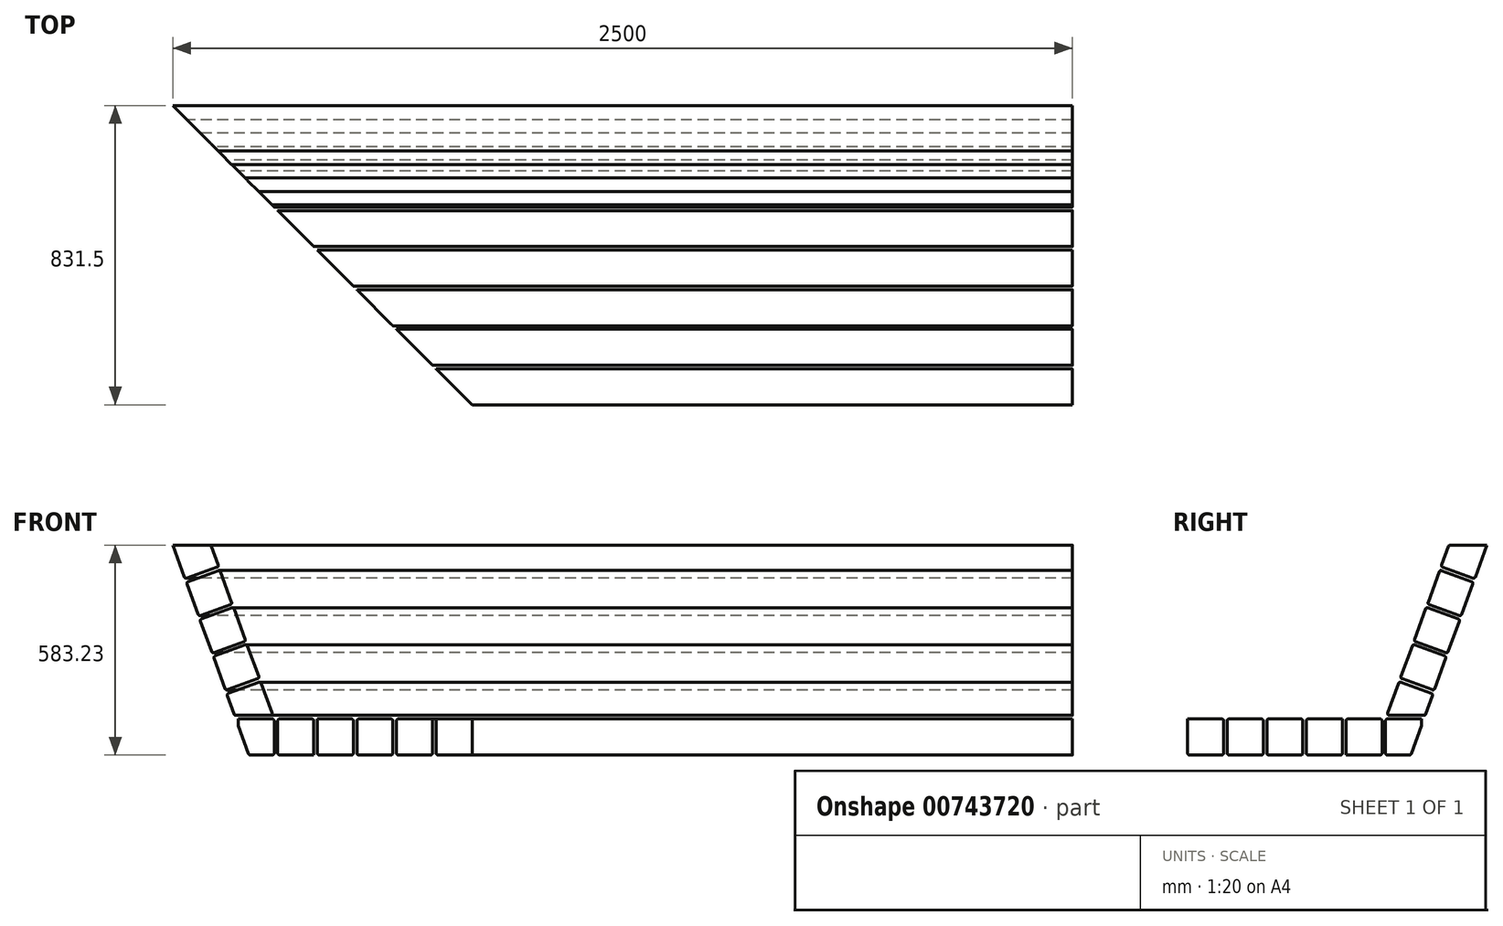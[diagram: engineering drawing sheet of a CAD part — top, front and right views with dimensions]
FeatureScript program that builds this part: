
annotation { "Feature Type Name" : "Feature", "Feature Type Description" : "" }
export const myFeature = defineFeature(function(context is Context, id is Id, definition is map)
    precondition{}
    {
        {
            var Q0;
            Q0=qCreatedBy(makeId("Right.planeOp"),FACE);
            var sketch = newSketch(context, id + "F0", { "sketchPlane" : qUnion([Q0])});
            skLineSegment(sketch, "E0.bottom", {"start": v(0, 0) * mm, "end": v(-95, 0) * mm});
            skLineSegment(sketch, "E0.top", {"start": v(-33.48, -100) * mm, "end": v(-95, -100) * mm});
            skLineSegment(sketch, "E0.left", {"start": v(0, 0) * mm, "end": v(0, -16.75) * mm});
            skLineSegment(sketch, "E0.right", {"start": v(-100, -5) * mm, "end": v(-100, -95) * mm});
            skLineSegment(sketch, "E1.1.0.0", {"start": v(-115, 0) * mm, "end": v(-205, 0) * mm});
            skLineSegment(sketch, "E1.1.0.1", {"start": v(-210, -5) * mm, "end": v(-210, -100) * mm});
            skLineSegment(sketch, "E1.1.0.2", {"start": v(-115, -100) * mm, "end": v(-210, -100) * mm});
            skLineSegment(sketch, "E1.1.0.3", {"start": v(-110, -5) * mm, "end": v(-110, -95) * mm});
            skLineSegment(sketch, "E1.2.0.0", {"start": v(-220, 0) * mm, "end": v(-315, 0) * mm});
            skLineSegment(sketch, "E1.2.0.1", {"start": v(-320, -5) * mm, "end": v(-320, -95) * mm});
            skLineSegment(sketch, "E1.2.0.2", {"start": v(-225, -100) * mm, "end": v(-315, -100) * mm});
            skLineSegment(sketch, "E1.2.0.3", {"start": v(-220, 0) * mm, "end": v(-220, -95) * mm});
            skLineSegment(sketch, "E1.3.0.0", {"start": v(-335, 0) * mm, "end": v(-425, 0) * mm});
            skLineSegment(sketch, "E1.3.0.1", {"start": v(-430, -5) * mm, "end": v(-430, -95) * mm});
            skLineSegment(sketch, "E1.3.0.2", {"start": v(-335, -100) * mm, "end": v(-425, -100) * mm});
            skLineSegment(sketch, "E1.3.0.3", {"start": v(-330, -5) * mm, "end": v(-330, -95) * mm});
            skLineSegment(sketch, "E1.4.0.0", {"start": v(-445, 0) * mm, "end": v(-535, 0) * mm});
            skLineSegment(sketch, "E1.4.0.1", {"start": v(-540, -5) * mm, "end": v(-540, -95) * mm});
            skLineSegment(sketch, "E1.4.0.2", {"start": v(-445, -100) * mm, "end": v(-535, -100) * mm});
            skLineSegment(sketch, "E1.4.0.3", {"start": v(-440, -5) * mm, "end": v(-440, -95) * mm});
            skLineSegment(sketch, "E1.5.0.0", {"start": v(-555, 0) * mm, "end": v(-650, 0) * mm});
            skLineSegment(sketch, "E1.5.0.1", {"start": v(-650, 0) * mm, "end": v(-650, -95) * mm});
            skLineSegment(sketch, "E1.5.0.2", {"start": v(-555, -100) * mm, "end": v(-645, -100) * mm});
            skLineSegment(sketch, "E1.5.0.3", {"start": v(-550, -5) * mm, "end": v(-550, -95) * mm});
            skLineSegment(sketch, "E1.direction1", {"start": v(-100, 0) * mm, "end": v(-210, 0) * mm, "construction": true});
            skLineSegment(sketch, "E2", {"start": v(-93.92, 16.71) * mm, "end": v(-63.87, 99.27) * mm});
            skLineSegment(sketch, "E3", {"start": v(-89.22, 10) * mm, "end": v(6.56, 10) * mm});
            skLineSegment(sketch, "E4", {"start": v(-57.46, 102.26) * mm, "end": v(27.11, 71.48) * mm});
            skLineSegment(sketch, "E5", {"start": v(30.1, 65.07) * mm, "end": v(11.25, 13.29) * mm});
            skPoint(sketch, "E6.orphan", {"position": v(0, -17.63) * mm});
            skLineSegment(sketch, "E7", {"start": v(-54.04, 111.66) * mm, "end": v(29.82, 81.13) * mm});
            skLineSegment(sketch, "E8", {"start": v(36.23, 84.12) * mm, "end": v(67.01, 168.7) * mm});
            skLineSegment(sketch, "E9", {"start": v(64.03, 175.1) * mm, "end": v(-19.84, 205.63) * mm});
            skLineSegment(sketch, "E10.trimOffspring", {"start": v(-57.03, 118.06) * mm, "end": v(-26.25, 202.64) * mm});
            skLineSegment(sketch, "E11", {"start": v(-19.4, 221.43) * mm, "end": v(11.38, 306) * mm});
            skLineSegment(sketch, "E12", {"start": v(181.55, 483.38) * mm, "end": v(149.1, 394.22) * mm});
            skLineSegment(sketch, "E13", {"start": v(-16.42, 215.02) * mm, "end": v(67.45, 184.5) * mm});
            skLineSegment(sketch, "E14", {"start": v(17.78, 309) * mm, "end": v(101.65, 278.47) * mm});
            skLineSegment(sketch, "E15", {"start": v(21.2, 318.39) * mm, "end": v(105.07, 287.86) * mm});
            skLineSegment(sketch, "E16", {"start": v(55.4, 412.36) * mm, "end": v(139.27, 381.83) * mm});
            skLineSegment(sketch, "E17", {"start": v(58.83, 421.75) * mm, "end": v(142.7, 391.23) * mm});
            skLineSegment(sketch, "E18", {"start": v(181.5, 483.23) * mm, "end": v(79.38, 483.23) * mm});
            skLineSegment(sketch, "E19.trimOffspring", {"start": v(142.26, 375.43) * mm, "end": v(111.48, 290.85) * mm});
            skLineSegment(sketch, "E20.trimOffspring", {"start": v(55.84, 428.16) * mm, "end": v(74.68, 479.94) * mm});
            skLineSegment(sketch, "E21.trimOffspring", {"start": v(18.22, 324.8) * mm, "end": v(49, 409.37) * mm});
            skLineSegment(sketch, "E22.trimOffspring", {"start": v(104.64, 272.06) * mm, "end": v(73.85, 187.49) * mm});
            skLineSegment(sketch, "E23", {"start": v(-0.3, -18.46) * mm, "end": v(-28.78, -96.71) * mm});
            skPoint(sketch, "E24.orphan", {"position": v(0, -100) * mm});
            skArc(sketch, "E25.filletArc", {"start": v(-650, -95) * mm, "mid": v(-648.54, -98.54) * mm, "end": v(-645, -100) * mm});
            skPoint(sketch, "E26.visualSharp", {"position": v(-550, -100) * mm});
            skArc(sketch, "E26.filletArc", {"start": v(-555, -100) * mm, "mid": v(-551.46, -98.54) * mm, "end": v(-550, -95) * mm});
            skPoint(sketch, "E27.visualSharp", {"position": v(-550, 0) * mm});
            skArc(sketch, "E27.filletArc", {"start": v(-550, -5) * mm, "mid": v(-551.46, -1.46) * mm, "end": v(-555, 0) * mm});
            skPoint(sketch, "E28.visualSharp", {"position": v(-540, 0) * mm});
            skArc(sketch, "E28.filletArc", {"start": v(-535, 0) * mm, "mid": v(-538.54, -1.46) * mm, "end": v(-540, -5) * mm});
            skPoint(sketch, "E29.visualSharp", {"position": v(-540, -100) * mm});
            skArc(sketch, "E29.filletArc", {"start": v(-540, -95) * mm, "mid": v(-538.54, -98.54) * mm, "end": v(-535, -100) * mm});
            skPoint(sketch, "E30.visualSharp", {"position": v(-440, 0) * mm});
            skArc(sketch, "E30.filletArc", {"start": v(-440, -5) * mm, "mid": v(-441.46, -1.46) * mm, "end": v(-445, 0) * mm});
            skPoint(sketch, "E31.visualSharp", {"position": v(-430, 0) * mm});
            skArc(sketch, "E31.filletArc", {"start": v(-425, 0) * mm, "mid": v(-428.54, -1.46) * mm, "end": v(-430, -5) * mm});
            skPoint(sketch, "E32.visualSharp", {"position": v(-440, -100) * mm});
            skArc(sketch, "E32.filletArc", {"start": v(-445, -100) * mm, "mid": v(-441.46, -98.54) * mm, "end": v(-440, -95) * mm});
            skPoint(sketch, "E33.visualSharp", {"position": v(-430, -100) * mm});
            skArc(sketch, "E33.filletArc", {"start": v(-430, -95) * mm, "mid": v(-428.54, -98.54) * mm, "end": v(-425, -100) * mm});
            skPoint(sketch, "E34.visualSharp", {"position": v(-330, 0) * mm});
            skArc(sketch, "E34.filletArc", {"start": v(-330, -5) * mm, "mid": v(-331.46, -1.46) * mm, "end": v(-335, 0) * mm});
            skPoint(sketch, "E35.visualSharp", {"position": v(-330, -100) * mm});
            skArc(sketch, "E35.filletArc", {"start": v(-335, -100) * mm, "mid": v(-331.46, -98.54) * mm, "end": v(-330, -95) * mm});
            skPoint(sketch, "E36.visualSharp", {"position": v(-320, 0) * mm});
            skArc(sketch, "E36.filletArc", {"start": v(-315, 0) * mm, "mid": v(-318.54, -1.46) * mm, "end": v(-320, -5) * mm});
            skPoint(sketch, "E37.visualSharp", {"position": v(-320, -100) * mm});
            skArc(sketch, "E37.filletArc", {"start": v(-320, -95) * mm, "mid": v(-318.54, -98.54) * mm, "end": v(-315, -100) * mm});
            skPoint(sketch, "E38.visualSharp", {"position": v(-220, -100) * mm});
            skArc(sketch, "E38.filletArc", {"start": v(-225, -100) * mm, "mid": v(-221.46, -98.54) * mm, "end": v(-220, -95) * mm});
            skPoint(sketch, "E39.visualSharp", {"position": v(-210, 0) * mm});
            skArc(sketch, "E39.filletArc", {"start": v(-205, 0) * mm, "mid": v(-208.54, -1.46) * mm, "end": v(-210, -5) * mm});
            skPoint(sketch, "E40.visualSharp", {"position": v(-110, -100) * mm});
            skArc(sketch, "E40.filletArc", {"start": v(-115, -100) * mm, "mid": v(-111.46, -98.54) * mm, "end": v(-110, -95) * mm});
            skPoint(sketch, "E41.visualSharp", {"position": v(-110, 0) * mm});
            skArc(sketch, "E41.filletArc", {"start": v(-110, -5) * mm, "mid": v(-111.46, -1.46) * mm, "end": v(-115, 0) * mm});
            skPoint(sketch, "E42.visualSharp", {"position": v(-100, -100) * mm});
            skArc(sketch, "E42.filletArc", {"start": v(-100, -95) * mm, "mid": v(-98.54, -98.54) * mm, "end": v(-95, -100) * mm});
            skPoint(sketch, "E43.visualSharp", {"position": v(-29.98, -100) * mm});
            skArc(sketch, "E43.filletArc", {"start": v(-33.48, -100) * mm, "mid": v(-30.61, -99.1) * mm, "end": v(-28.78, -96.71) * mm});
            skPoint(sketch, "E44.visualSharp", {"position": v(-100, 0) * mm});
            skArc(sketch, "E44.filletArc", {"start": v(-95, 0) * mm, "mid": v(-98.54, -1.46) * mm, "end": v(-100, -5) * mm});
            skArc(sketch, "E45.filletArc", {"start": v(-0.3, -18.46) * mm, "mid": v(-0.08, -17.62) * mm, "end": v(0, -16.75) * mm});
            skPoint(sketch, "E46.visualSharp", {"position": v(-96.36, 10) * mm});
            skArc(sketch, "E46.filletArc", {"start": v(-93.92, 16.71) * mm, "mid": v(-93.32, 12.13) * mm, "end": v(-89.22, 10) * mm});
            skPoint(sketch, "E47.visualSharp", {"position": v(10.06, 10) * mm});
            skArc(sketch, "E47.filletArc", {"start": v(6.56, 10) * mm, "mid": v(9.42, 10.9) * mm, "end": v(11.25, 13.29) * mm});
            skPoint(sketch, "E48.visualSharp", {"position": v(-62.16, 103.97) * mm});
            skArc(sketch, "E48.filletArc", {"start": v(-57.46, 102.26) * mm, "mid": v(-61.28, 102.1) * mm, "end": v(-63.87, 99.27) * mm});
            skPoint(sketch, "E49.visualSharp", {"position": v(34.52, 79.42) * mm});
            skArc(sketch, "E49.filletArc", {"start": v(29.82, 81.13) * mm, "mid": v(33.65, 81.3) * mm, "end": v(36.23, 84.12) * mm});
            skPoint(sketch, "E50.visualSharp", {"position": v(-58.74, 113.37) * mm});
            skArc(sketch, "E50.filletArc", {"start": v(-57.03, 118.06) * mm, "mid": v(-56.86, 114.24) * mm, "end": v(-54.04, 111.66) * mm});
            skPoint(sketch, "E51.visualSharp", {"position": v(31.81, 69.77) * mm});
            skArc(sketch, "E51.filletArc", {"start": v(30.1, 65.07) * mm, "mid": v(29.93, 68.9) * mm, "end": v(27.11, 71.48) * mm});
            skPoint(sketch, "E52.visualSharp", {"position": v(68.72, 173.4) * mm});
            skArc(sketch, "E52.filletArc", {"start": v(67.01, 168.7) * mm, "mid": v(66.85, 172.52) * mm, "end": v(64.03, 175.1) * mm});
            skPoint(sketch, "E53.visualSharp", {"position": v(-21.12, 216.73) * mm});
            skArc(sketch, "E53.filletArc", {"start": v(-19.4, 221.43) * mm, "mid": v(-19.24, 217.6) * mm, "end": v(-16.42, 215.02) * mm});
            skPoint(sketch, "E54.visualSharp", {"position": v(-24.54, 207.34) * mm});
            skArc(sketch, "E54.filletArc", {"start": v(-19.84, 205.63) * mm, "mid": v(-23.66, 205.46) * mm, "end": v(-26.25, 202.64) * mm});
            skPoint(sketch, "E55.visualSharp", {"position": v(72.14, 182.79) * mm});
            skArc(sketch, "E55.filletArc", {"start": v(67.45, 184.5) * mm, "mid": v(71.27, 184.67) * mm, "end": v(73.85, 187.49) * mm});
            skPoint(sketch, "E56.visualSharp", {"position": v(106.35, 276.76) * mm});
            skArc(sketch, "E56.filletArc", {"start": v(104.64, 272.06) * mm, "mid": v(104.47, 275.88) * mm, "end": v(101.65, 278.47) * mm});
            skPoint(sketch, "E57.visualSharp", {"position": v(109.77, 286.15) * mm});
            skArc(sketch, "E57.filletArc", {"start": v(105.07, 287.86) * mm, "mid": v(108.9, 288.03) * mm, "end": v(111.48, 290.85) * mm});
            skPoint(sketch, "E58.visualSharp", {"position": v(16.5, 320.1) * mm});
            skArc(sketch, "E58.filletArc", {"start": v(18.22, 324.8) * mm, "mid": v(18.38, 320.97) * mm, "end": v(21.2, 318.39) * mm});
            skPoint(sketch, "E59.visualSharp", {"position": v(13.09, 310.7) * mm});
            skArc(sketch, "E59.filletArc", {"start": v(17.78, 309) * mm, "mid": v(13.96, 308.82) * mm, "end": v(11.38, 306) * mm});
            skPoint(sketch, "E60.visualSharp", {"position": v(143.97, 380.12) * mm});
            skArc(sketch, "E60.filletArc", {"start": v(142.26, 375.43) * mm, "mid": v(142.1, 379.25) * mm, "end": v(139.27, 381.83) * mm});
            skPoint(sketch, "E61.visualSharp", {"position": v(54.13, 423.46) * mm});
            skArc(sketch, "E61.filletArc", {"start": v(55.84, 428.16) * mm, "mid": v(56, 424.34) * mm, "end": v(58.83, 421.75) * mm});
            skPoint(sketch, "E62.visualSharp", {"position": v(181.5, 483.23) * mm});
            skPoint(sketch, "E63.visualSharp", {"position": v(147.39, 389.52) * mm});
            skArc(sketch, "E63.filletArc", {"start": v(142.7, 391.23) * mm, "mid": v(146.51, 391.4) * mm, "end": v(149.1, 394.22) * mm});
            skPoint(sketch, "E64.visualSharp", {"position": v(50.7, 414.07) * mm});
            skArc(sketch, "E64.filletArc", {"start": v(55.4, 412.36) * mm, "mid": v(51.58, 412.2) * mm, "end": v(49, 409.37) * mm});
            skPoint(sketch, "E65.visualSharp", {"position": v(75.88, 483.23) * mm});
            skArc(sketch, "E65.filletArc", {"start": v(79.38, 483.23) * mm, "mid": v(76.52, 482.33) * mm, "end": v(74.68, 479.94) * mm});
            skSolve(sketch);
        }
        {
            var Q0;
            Q0=makeQuery(id+"F0.imprint","IMPRINT",FACE,{"disambiguationData":[TD([[makeQuery(id+"F0.imprint","IMPRINT",EDGE,{"derivedFrom":sQuery(id+"F0.wireOp",EDGE,"E1.6.0.0")}),1.0]])]});
            var Q1;
            Q1 = qSketchRegion(id + "F0", true);
            extrude(context, id + "F1", {"entities" : qUnion([Q0, Q1]), "depth" : 2500 * mm, "offsetDistance" : 25 * mm});
        }
        {
            var Q0;
            Q0=makeQuery(id+"F1.opExtrude","SWEPT_FACE",FACE,{"disambiguationData":[OSD([sQuery(id+"F0.wireOp",EDGE,"E18")])]});
            var sketch = newSketch(context, id + "F2", { "sketchPlane" : qUnion([Q0])});
            skLineSegment(sketch, "E66.top", {"start": v(0, -651) * mm, "end": v(832.5, -651) * mm});
            skLineSegment(sketch, "E66.left", {"start": v(0, 181.5) * mm, "end": v(0, -651) * mm});
            skLineSegment(sketch, "E67", {"start": v(0, 181.5) * mm, "end": v(832.5, -651) * mm});
            skSolve(sketch);
        }
        {
            var Q0;
            {var subQ1=sQuery(id+"F2.wireOp",EDGE,"E66.left");var subQ2=sQuery(id+"F0.wireOp",EDGE,"E18");var subQ4=makeQuery(id+"F1.opExtrude","SWEPT_EDGE",EDGE,{"disambiguationData":[OSD([subQ2,sQuery(id+"F0.wireOp",EDGE,"E65.filletArc")])]});var subQ5=makeQuery(id+"F2.imprint","INTERSECT",VERTEX,{"derivedFrom":[subQ4,subQ1]});Q0=makeQuery(id+"F2.imprint","IMPRINT",FACE,{"disambiguationData":[TD([[makeQuery(id+"F2.imprint","IMPRINT",EDGE,{"disambiguationData":[TD([[subQ5,1.0]])],"derivedFrom":subQ1}),1.0]])]});}
            var Q1;
            {var subQ0=sQuery(id+"F2.wireOp",EDGE,"E66.top");Q1=makeQuery(id+"F2.imprint","IMPRINT",FACE,{"disambiguationData":[TD([[makeQuery(id+"F2.imprint","IMPRINT",EDGE,{"derivedFrom":subQ0}),1.0]])]});}
            var Q2;
            Q2=makeQuery(id+"F1.opExtrude","SWEPT_FACE",FACE,{"disambiguationData":[OSD([sQuery(id+"F0.wireOp",EDGE,"E1.4.0.2")])]});
            extrude(context, id + "F3", {"entities" : qUnion([Q0, Q1]), "operationType" : NewBodyOperationType.REMOVE, "endBound" : BoundingType.THROUGH_ALL, "oppositeDirection" : true, "depth" : 711 * mm, "endBoundEntityFace" : qUnion([Q2]), "offsetDistance" : 25 * mm});
        }
    });
